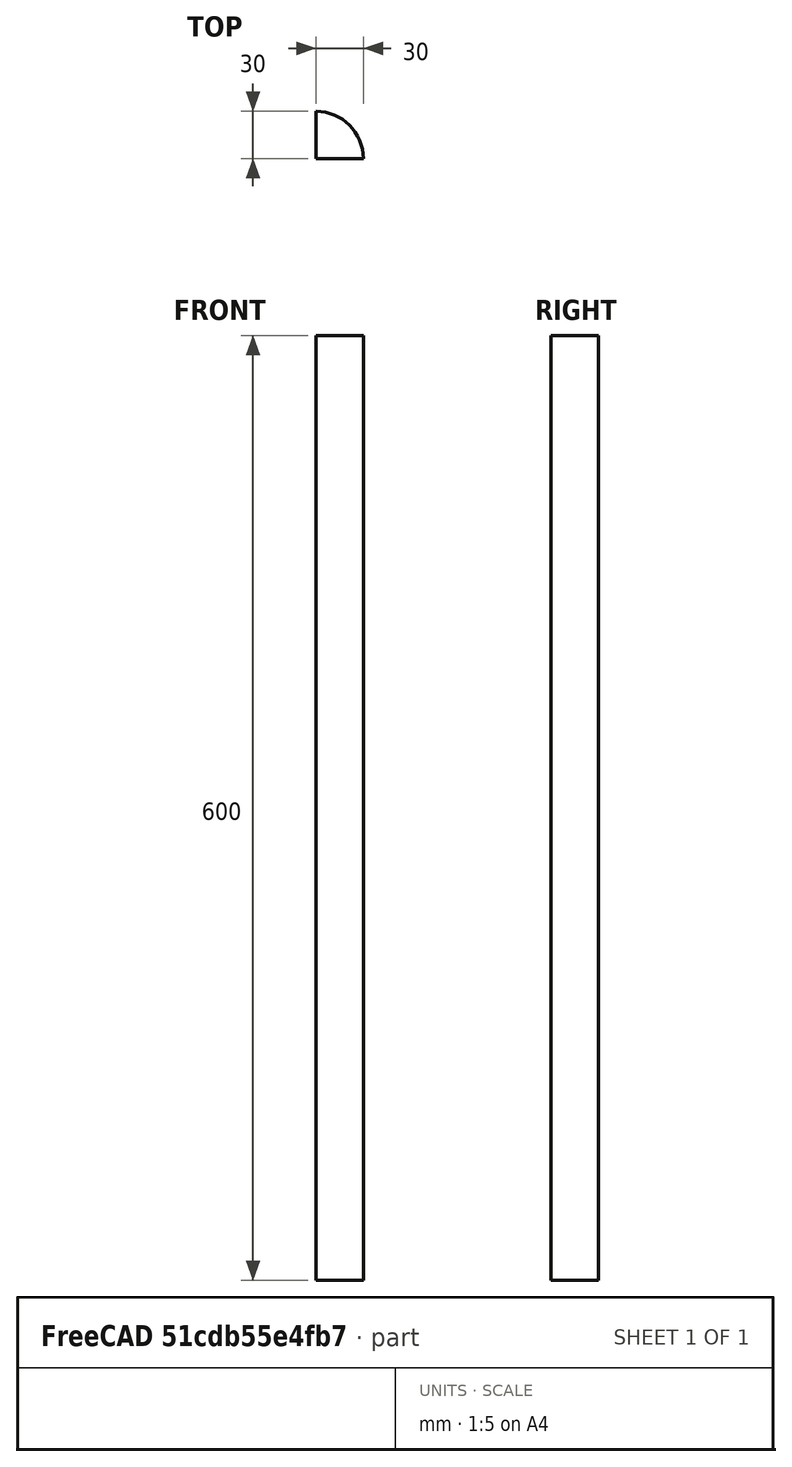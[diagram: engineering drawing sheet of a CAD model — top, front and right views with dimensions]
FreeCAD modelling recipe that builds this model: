
FCSTD DOCUMENT  (FreeCAD 0.16R6703 (Git))
Label: lunar_base_rod
License: Public Domain
LicenseURL: http://en.wikipedia.org/wiki/Public_domain
objects: Sketcher::SketchObject×1, PartDesign::Pad×1
note: 3 computed .brp shape members not serialized (recipe doc carries the construction recipe); baked Part::Feature solids carry a one-line shape summary decoded from their .brp

FEATURE [Sketcher::SketchObject] Sketch001
  sketch-geometry (3):
    g0: ArcOfCircle CenterX=0 CenterY=0 CenterZ=0 NormalX=0 NormalY=0 NormalZ=1 Radius=30 StartAngle=0 EndAngle=1.5708
    g1: LineSegment StartX=0 StartY=30 StartZ=0 EndX=0 EndY=0 EndZ=0
    g2: LineSegment StartX=0 StartY=0 StartZ=0 EndX=30 EndY=0 EndZ=0
  constraints (8):
    c: Coincident(g0,g-1)
    c: PointOnObject(g0,g-2)
    c: PointOnObject(g0,g-1)
    c: Coincident(g1,g0)
    c: Coincident(g2,g1)
    c: Coincident(g2,g0)
    c: Coincident(g0,g1)
    c: DistanceX(g2,g2) = 30
FEATURE [PartDesign::Pad] Pad001  label="rod"
  Length = 600
  Length2 = 100
  Sketch = -> Sketch001
  Type = 0
